# Revit family: Sanitary_Toilets_TOTO-USA-Inc_SPT-Wall-Hung-Toilet
name_source: partatom
category: Plumbing Fixtures
revit_build: Autodesk Revit 2015 (Build: 20140606_1530(x64)
units: mm (PartAtom-declared; Revit-internal decimal feet)

## types (1)
- CT449CFG
    BIMobject category = Toilets
    BIMobject category code = sanitary-toilets
    BIMobject main category = Sanitary
    BIMobject main category code = sanitary
    Brand url = https://www.totousa.com
    Default Elevation = 1' - 6"
    Description = With a new modern square shape, the SP wall-hung toilet saves valuable bathroom space while delivering a contemporary bathroom style.
    Edition number = 1
    IFC Classification = Flow Terminal
    Installation instructions = https://www.totousa.com
    Manufacturer = TOTO
    Manufacturer name = TOTO USA Inc
    Masterformat 2014 Code = 10 28 00
    Masterformat 2014 Description = Toilet, Bath, and Laundry Accessories
    Material = Galaline - TOTO - Reinforced Marble
    Material main = Ceramics
    Model = CT449CFG
    Nominal height = 0' - 0"
    Nominal width = 0' - 0"
    OmniClass Code = 23-31 19 00
    OmniClass Description = Toilets
    Product Guid = 61059e5c-7e90-458f-ac29-6402b5300402
    Product SKU = toto-ct449cfg
    Product certification = https://www.totousa.com
    Product data url = https://bimobject.com
    Product family = Urinals
    Product group = SP???
    Product url = https://www.totousa.com
    QR code = http://bimobject.com
    Technical description = https://www.totousa.com
    Trap Seal = 0' - 2"
    Trap diameter = 0' - 2"
    UNSPSC Code = 30181505
    URL = www.totousa.com
    Uniclass 1.4 Code = L7216
    Uniclass 1.4 Description = Toilets
    Uniclass 2.0 Code = SS-35-65-90
    Uniclass 2.0 Description = Toilet Systems
    Uniclass 2015 Code = SL_35_80_89
    Uniclass 2015 Name = Toilets
    Uniformat II Code = D2030
    Uniformat II Description = Sanitary Waste
    Warranty = One Year Limited

## geometry (parser evidence)
native form markers: Blend x4, Sweep x2
no freeform markers — native parametric forms only
